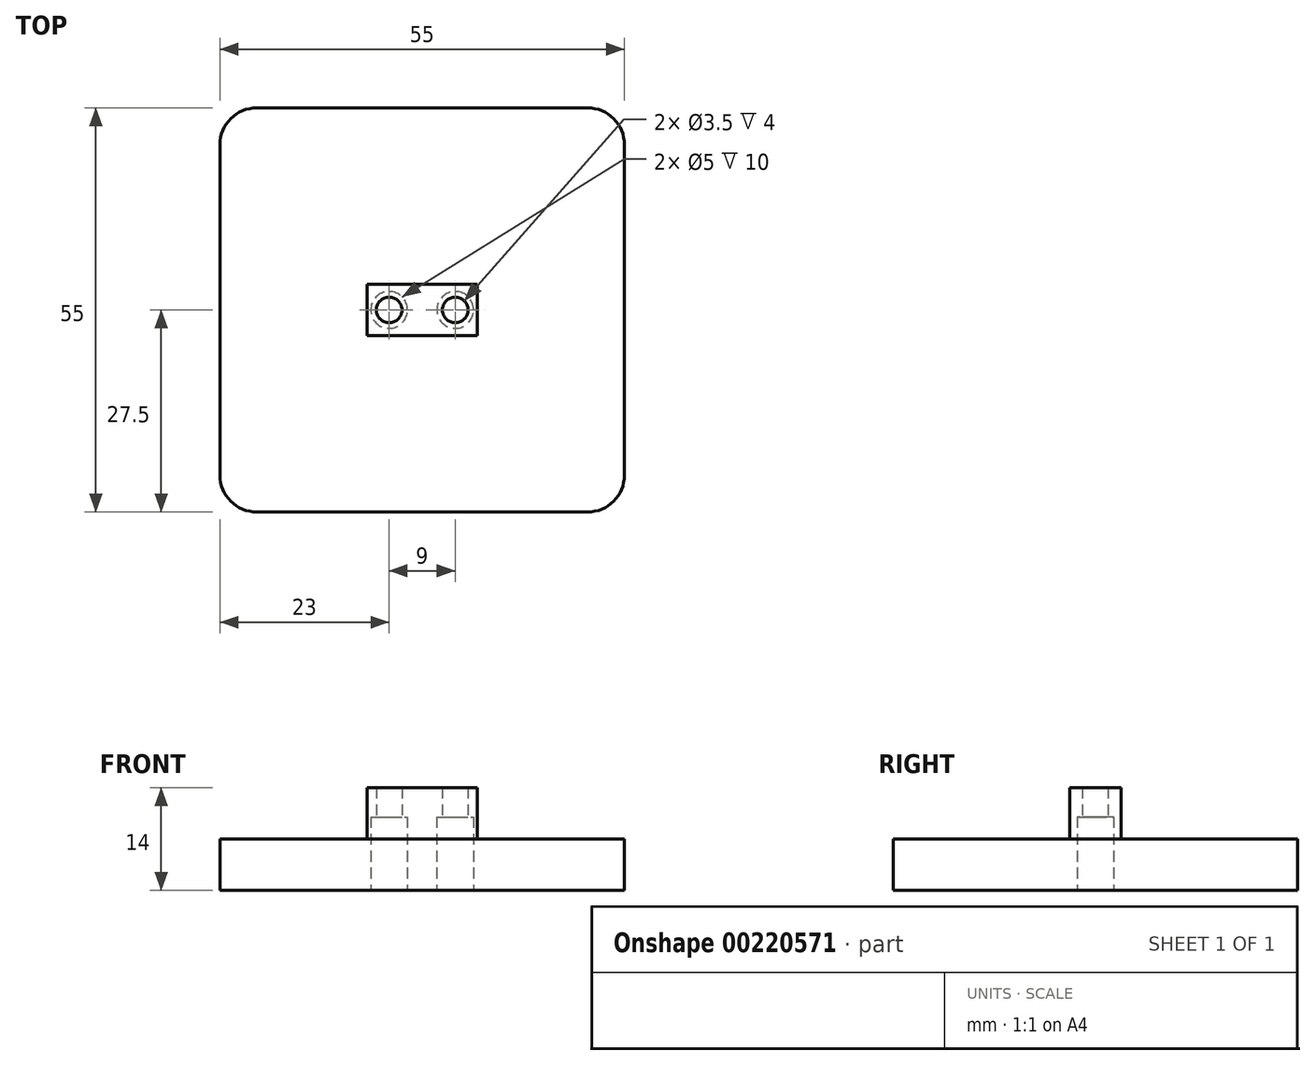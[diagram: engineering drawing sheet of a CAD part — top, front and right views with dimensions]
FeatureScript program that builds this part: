
annotation { "Feature Type Name" : "Feature", "Feature Type Description" : "" }
export const myFeature = defineFeature(function(context is Context, id is Id, definition is map)
    precondition{}
    {
        {
            var Q0;
            Q0=qCreatedBy(makeId("Top.planeOp"),FACE);
            var sketch = newSketch(context, id + "F0", { "sketchPlane" : qUnion([Q0])});
            skLineSegment(sketch, "E0.bottom", {"start": v(22.5, 27.5) * mm, "end": v(-22.5, 27.5) * mm});
            skLineSegment(sketch, "E0.top", {"start": v(22.5, -27.5) * mm, "end": v(-22.5, -27.5) * mm});
            skLineSegment(sketch, "E0.left", {"start": v(27.5, 22.5) * mm, "end": v(27.5, -22.5) * mm});
            skLineSegment(sketch, "E0.right", {"start": v(-27.5, 22.5) * mm, "end": v(-27.5, -22.5) * mm});
            skPoint(sketch, "E0.middle", {"position": v(0, 0) * mm});
            skPoint(sketch, "E1.visualSharp", {"position": v(-27.5, 27.5) * mm});
            skArc(sketch, "E1.filletArc", {"start": v(-22.5, 27.5) * mm, "mid": v(-26.04, 26.04) * mm, "end": v(-27.5, 22.5) * mm});
            skPoint(sketch, "E2.visualSharp", {"position": v(27.5, 27.5) * mm});
            skArc(sketch, "E2.filletArc", {"start": v(27.5, 22.5) * mm, "mid": v(26.04, 26.04) * mm, "end": v(22.5, 27.5) * mm});
            skPoint(sketch, "E3.visualSharp", {"position": v(27.5, -27.5) * mm});
            skArc(sketch, "E3.filletArc", {"start": v(22.5, -27.5) * mm, "mid": v(26.04, -26.04) * mm, "end": v(27.5, -22.5) * mm});
            skPoint(sketch, "E4.visualSharp", {"position": v(-27.5, -27.5) * mm});
            skArc(sketch, "E4.filletArc", {"start": v(-27.5, -22.5) * mm, "mid": v(-26.04, -26.04) * mm, "end": v(-22.5, -27.5) * mm});
            skSolve(sketch);
        }
        {
            var Q0;
            Q0=makeQuery(id+"F0.imprint","IMPRINT",FACE,{"disambiguationData":[TD([[makeQuery(id+"F0.imprint","IMPRINT",EDGE,{"derivedFrom":sQuery(id+"F0.wireOp",EDGE,"E0.bottom")}),1.0]])]});
            extrude(context, id + "F1", {"entities" : qUnion([Q0]), "depth" : 7 * mm});
        }
        {
            var Q0;
            Q0=makeQuery(id+"F1.opExtrude","CAP_FACE",FACE,{"disambiguationData":[OSD([sQuery(id+"F0.wireOp",EDGE,"E0.bottom"),sQuery(id+"F0.wireOp",EDGE,"E0.top"),sQuery(id+"F0.wireOp",EDGE,"E0.left"),sQuery(id+"F0.wireOp",EDGE,"E0.right"),sQuery(id+"F0.wireOp",EDGE,"E1.filletArc"),sQuery(id+"F0.wireOp",EDGE,"E2.filletArc"),sQuery(id+"F0.wireOp",EDGE,"E3.filletArc"),sQuery(id+"F0.wireOp",EDGE,"E4.filletArc")])],"isStart":false});
            var sketch = newSketch(context, id + "F2", { "sketchPlane" : qUnion([Q0])});
            skLineSegment(sketch, "E5.bottom", {"start": v(7.5, 3.5) * mm, "end": v(-7.5, 3.5) * mm});
            skLineSegment(sketch, "E5.top", {"start": v(7.5, -3.5) * mm, "end": v(-7.5, -3.5) * mm});
            skLineSegment(sketch, "E5.left", {"start": v(7.5, 3.5) * mm, "end": v(7.5, -3.5) * mm});
            skLineSegment(sketch, "E5.right", {"start": v(-7.5, 3.5) * mm, "end": v(-7.5, -3.5) * mm});
            skPoint(sketch, "E5.middle", {"position": v(0, 0) * mm});
            skLineSegment(sketch, "E6", {"start": v(0, 0) * mm, "end": v(-4.5, 0) * mm});
            skLineSegment(sketch, "E7", {"start": v(0, 0) * mm, "end": v(4.5, 0) * mm});
            skCircle(sketch, "E8", {"center": v(-4.5, 0) * mm, "radius": 1.75 * mm});
            skCircle(sketch, "E9", {"center": v(4.5, 0) * mm, "radius": 1.75 * mm});
            skSolve(sketch);
        }
        {
            var Q0;
            Q0=makeQuery(id+"F2.imprint","IMPRINT",FACE,{"disambiguationData":[TD([[makeQuery(id+"F2.imprint","IMPRINT",EDGE,{"derivedFrom":sQuery(id+"F2.wireOp",EDGE,"E5.bottom")}),1.0]])]});
            extrude(context, id + "F3", {"entities" : qUnion([Q0]), "operationType" : NewBodyOperationType.ADD, "depth" : 7 * mm});
        }
        {
            var Q0;
            Q0=makeQuery(id+"F1.opExtrude","CAP_FACE",FACE,{"disambiguationData":[OSD([sQuery(id+"F0.wireOp",EDGE,"E0.bottom"),sQuery(id+"F0.wireOp",EDGE,"E0.top"),sQuery(id+"F0.wireOp",EDGE,"E0.left"),sQuery(id+"F0.wireOp",EDGE,"E0.right"),sQuery(id+"F0.wireOp",EDGE,"E1.filletArc"),sQuery(id+"F0.wireOp",EDGE,"E2.filletArc"),sQuery(id+"F0.wireOp",EDGE,"E3.filletArc"),sQuery(id+"F0.wireOp",EDGE,"E4.filletArc")])],"isStart":true});
            var sketch = newSketch(context, id + "F4", { "sketchPlane" : qUnion([Q0])});
            skLineSegment(sketch, "E10", {"start": v(0, 0) * mm, "end": v(-4.5, 0) * mm});
            skLineSegment(sketch, "E11", {"start": v(0, 0) * mm, "end": v(4.5, 0) * mm});
            skCircle(sketch, "E12", {"center": v(4.5, 0) * mm, "radius": 2.5 * mm});
            skCircle(sketch, "E13", {"center": v(-4.5, 0) * mm, "radius": 2.5 * mm});
            skSolve(sketch);
        }
        {
            var Q0;
            Q0=makeQuery(id+"F4.imprint","IMPRINT",FACE,{"disambiguationData":[TD([[makeQuery(id+"F4.imprint","IMPRINT",EDGE,{"derivedFrom":sQuery(id+"F4.wireOp",EDGE,"E13")}),1.0]])]});
            var Q1;
            Q1=makeQuery(id+"F4.imprint","IMPRINT",FACE,{"disambiguationData":[TD([[makeQuery(id+"F4.imprint","IMPRINT",EDGE,{"derivedFrom":sQuery(id+"F4.wireOp",EDGE,"E12")}),1.0]])]});
            extrude(context, id + "F5", {"entities" : qUnion([Q0, Q1]), "operationType" : NewBodyOperationType.REMOVE, "oppositeDirection" : true, "depth" : 10 * mm});
        }
    });
